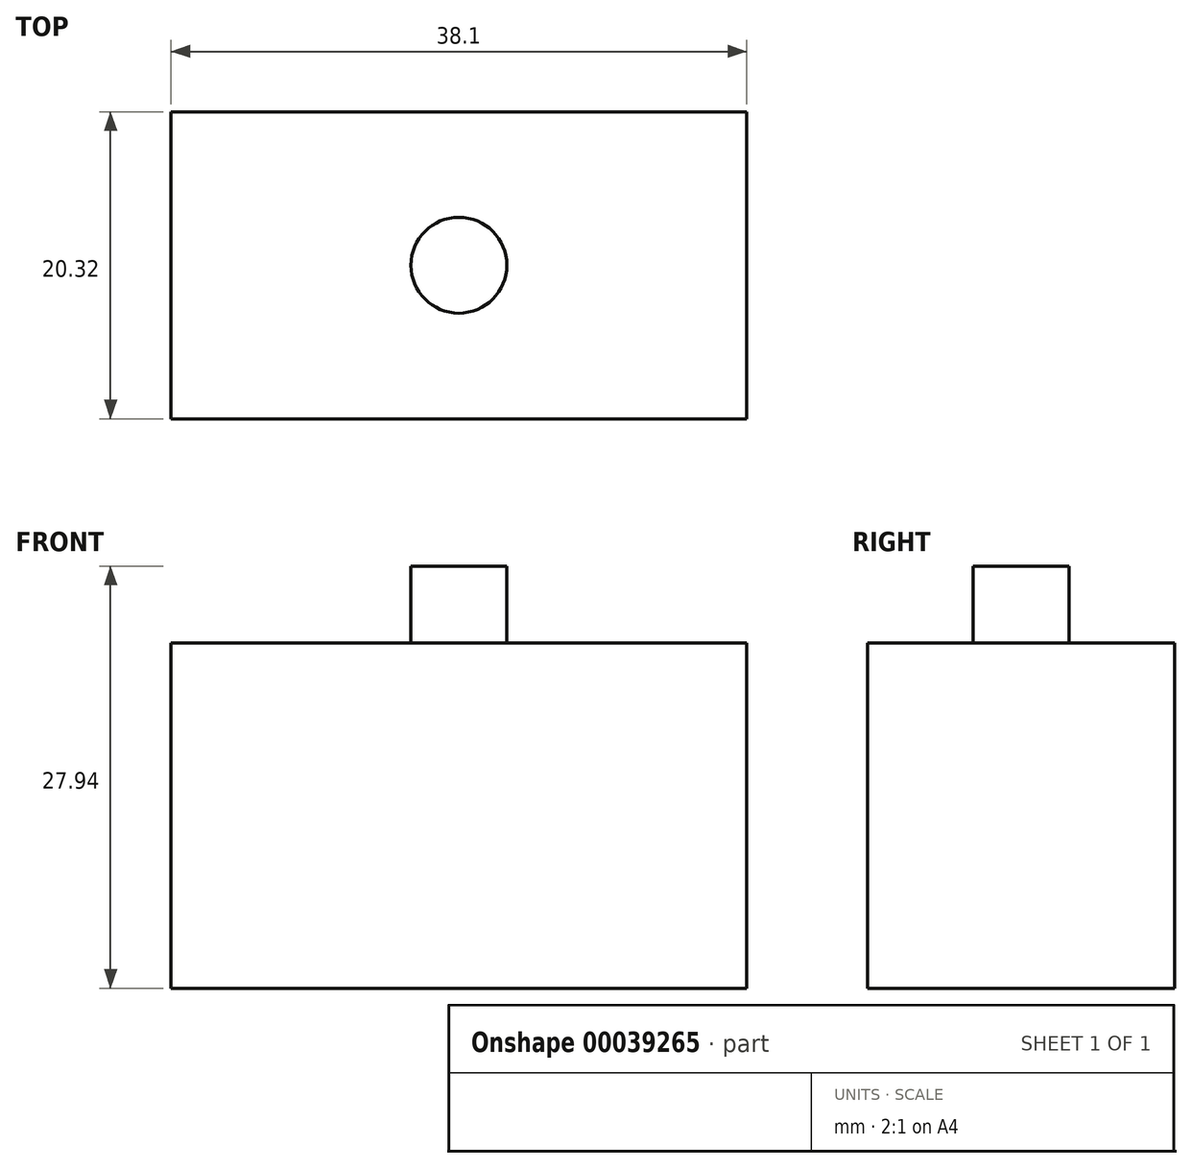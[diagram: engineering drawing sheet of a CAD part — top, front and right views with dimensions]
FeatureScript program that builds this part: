
annotation { "Feature Type Name" : "Feature", "Feature Type Description" : "" }
export const myFeature = defineFeature(function(context is Context, id is Id, definition is map)
    precondition{}
    {
        {
            var Q0;
            Q0=qCreatedBy(makeId("Top.planeOp"),FACE);
            var sketch = newSketch(context, id + "F0", { "sketchPlane" : qUnion([Q0])});
            skLineSegment(sketch, "E0.rect.bottom", {"start": v(19.05, 10.16) * mm, "end": v(-19.05, 10.16) * mm});
            skLineSegment(sketch, "E0.rect.top", {"start": v(19.05, -10.16) * mm, "end": v(-19.05, -10.16) * mm});
            skLineSegment(sketch, "E0.rect.left", {"start": v(19.05, 10.16) * mm, "end": v(19.05, -10.16) * mm});
            skLineSegment(sketch, "E0.rect.right", {"start": v(-19.05, 10.16) * mm, "end": v(-19.05, -10.16) * mm});
            skPoint(sketch, "E0.rect.middle", {"position": v(0, 0) * mm});
            skSolve(sketch);
        }
        {
            var Q0;
            Q0 = qSketchRegion(id + "F0", true);
            extrude(context, id + "F1", {"entities" : qUnion([Q0]), "depth" : 22.86 * mm});
        }
        {
            var Q0;
            Q0=makeQuery(id+"F1.opExtrude","CAP_FACE",FACE,{"disambiguationData":[OSD([sQuery(id+"F0.wireOp",EDGE,"E0.rect.bottom"),sQuery(id+"F0.wireOp",EDGE,"E0.rect.top"),sQuery(id+"F0.wireOp",EDGE,"E0.rect.left"),sQuery(id+"F0.wireOp",EDGE,"E0.rect.right")])],"isStart":false});
            var sketch = newSketch(context, id + "F2", { "sketchPlane" : qUnion([Q0])});
            skCircle(sketch, "E1", {"center": v(0, 0) * mm, "radius": 3.18 * mm});
            skSolve(sketch);
        }
        {
            var Q0;
            Q0 = qSketchRegion(id + "F2", true);
            extrude(context, id + "F3", {"entities" : qUnion([Q0]), "operationType" : NewBodyOperationType.ADD, "depth" : 5.08 * mm});
        }
    });
